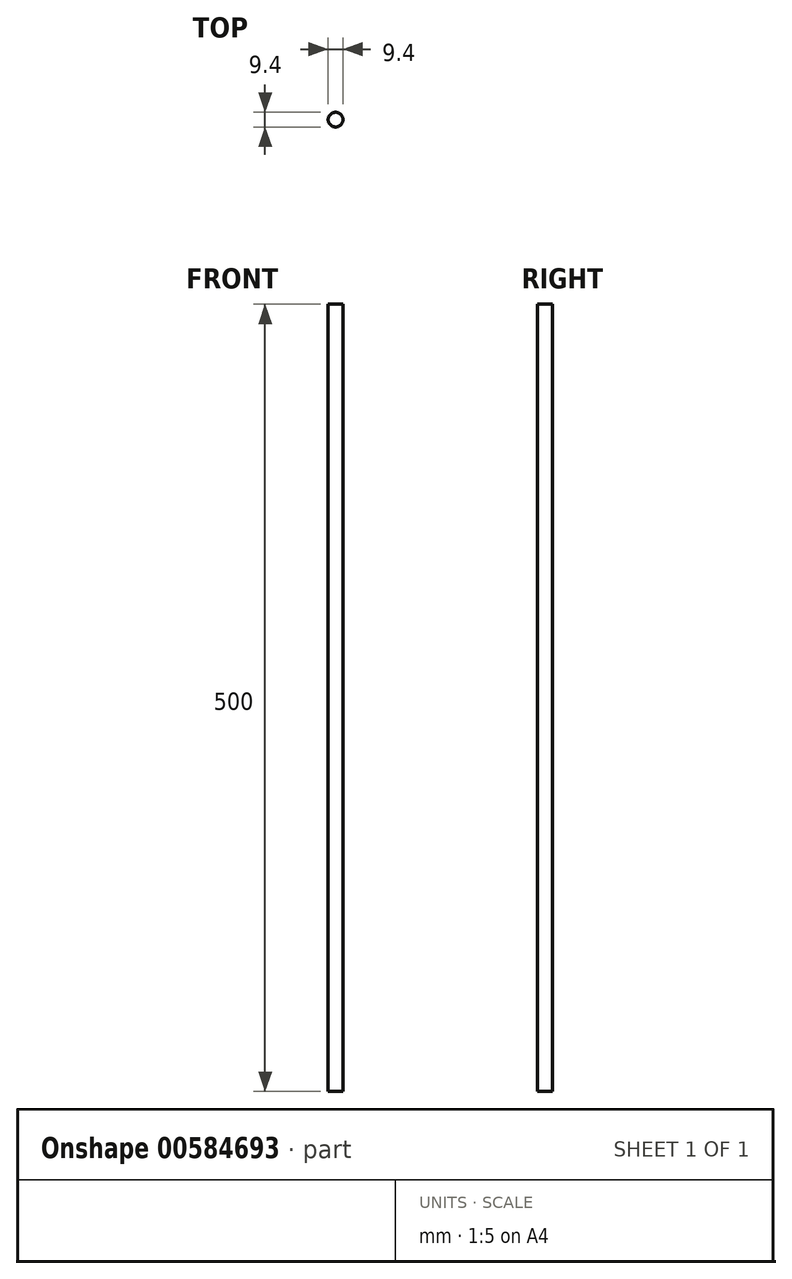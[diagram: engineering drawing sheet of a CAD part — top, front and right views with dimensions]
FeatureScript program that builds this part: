
annotation { "Feature Type Name" : "Feature", "Feature Type Description" : "" }
export const myFeature = defineFeature(function(context is Context, id is Id, definition is map)
    precondition{}
    {
        {
            var Q0;
            Q0=qCreatedBy(makeId("Top.planeOp"),FACE);
            var sketch = newSketch(context, id + "F0", { "sketchPlane" : qUnion([Q0])});
            skCircle(sketch, "E0", {"center": v(0, 0) * mm, "radius": 4.7 * mm});
            skSolve(sketch);
        }
        {
            var Q0;
            Q0 = qSketchRegion(id + "F0", true);
            extrude(context, id + "F1", {"entities" : qUnion([Q0]), "depth" : 500 * mm, "offsetDistance" : 25 * mm});
        }
    });
